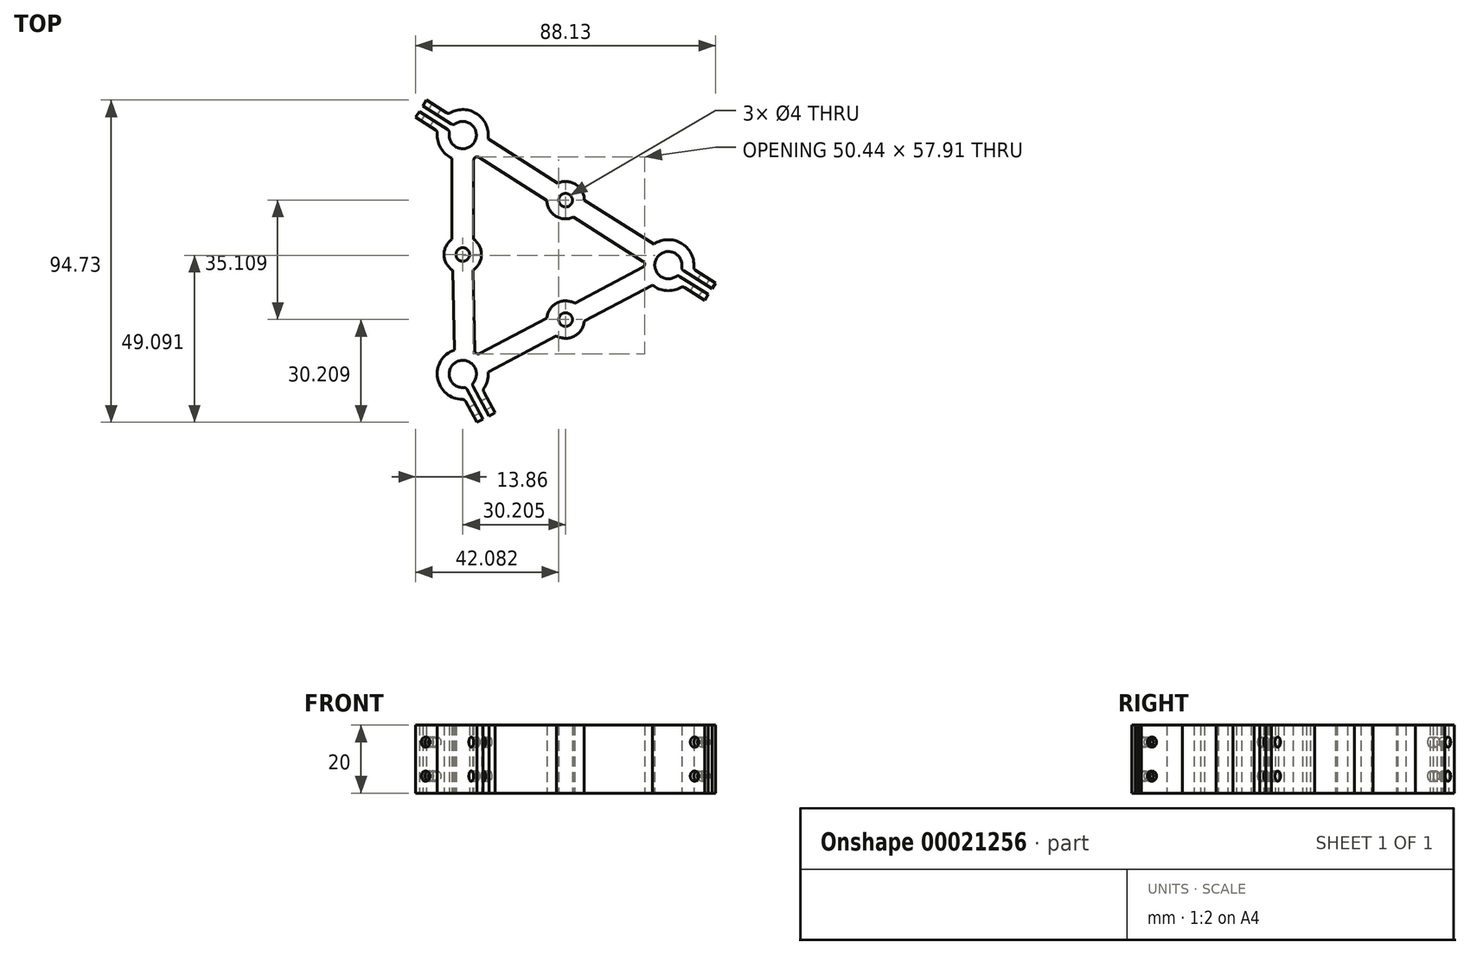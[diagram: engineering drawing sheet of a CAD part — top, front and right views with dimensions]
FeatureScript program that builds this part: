
annotation { "Feature Type Name" : "Feature", "Feature Type Description" : "" }
export const myFeature = defineFeature(function(context is Context, id is Id, definition is map)
    precondition{}
    {
        {
            var Q0;
            Q0=qCreatedBy(makeId("Top.planeOp"),FACE);
            var sketch = newSketch(context, id + "F0", { "sketchPlane" : qUnion([Q0])});
            skArc(sketch, "E0.0", {"start": v(64.36, 31.37) * mm, "mid": v(57.03, 34.12) * mm, "end": v(62.65, 28.66) * mm});
            skLineSegment(sketch, "E1", {"start": v(0, 0) * mm, "end": v(60.41, 31.98) * mm, "construction": true});
            skArc(sketch, "E2", {"start": v(3.13, -2.5) * mm, "mid": v(-1.87, 3.54) * mm, "end": v(0.3, -3.99) * mm});
            skArc(sketch, "E3", {"start": v(-3.95, 70.83) * mm, "mid": v(3.38, 68.08) * mm, "end": v(-2.24, 73.53) * mm});
            skLineSegment(sketch, "E4", {"start": v(60.41, 31.98) * mm, "end": v(0, 70.22) * mm, "construction": true});
            skCircle(sketch, "E5.0", {"center": v(30.2, 15.99) * mm, "radius": 2 * mm});
            skCircle(sketch, "E6.0", {"center": v(30.2, 51.1) * mm, "radius": 2 * mm});
            skArc(sketch, "E7.0", {"start": v(35.7, 51.17) * mm, "mid": v(33.15, 55.75) * mm, "end": v(27.91, 56.1) * mm});
            skLineSegment(sketch, "E8.0", {"start": v(56.2, 38.19) * mm, "end": v(35.7, 51.17) * mm});
            skLineSegment(sketch, "E9.0", {"start": v(52.98, 33.13) * mm, "end": v(32.5, 46.1) * mm});
            skArc(sketch, "E10.0", {"start": v(24.7, 51.03) * mm, "mid": v(27.26, 46.45) * mm, "end": v(32.5, 46.1) * mm});
            skLineSegment(sketch, "E11.0", {"start": v(24.7, 51.03) * mm, "end": v(4.73, 63.67) * mm});
            skLineSegment(sketch, "E12.0", {"start": v(27.91, 56.1) * mm, "end": v(7.41, 69.08) * mm});
            skLineSegment(sketch, "E13.0", {"start": v(7.48, 0.56) * mm, "end": v(27.53, 11.18) * mm});
            skArc(sketch, "E14.0", {"start": v(27.53, 11.18) * mm, "mid": v(32.78, 11.13) * mm, "end": v(35.68, 15.5) * mm});
            skArc(sketch, "E15.0", {"start": v(32.88, 20.8) * mm, "mid": v(27.63, 20.85) * mm, "end": v(24.73, 16.48) * mm});
            skLineSegment(sketch, "E16.0", {"start": v(35.68, 15.5) * mm, "end": v(55.74, 26.11) * mm});
            skLineSegment(sketch, "E17.0", {"start": v(52.91, 31.4) * mm, "end": v(32.88, 20.8) * mm});
            skLineSegment(sketch, "E18.0", {"start": v(-3, 30.5) * mm, "end": v(-2.5, 7.07) * mm});
            skArc(sketch, "E19.0", {"start": v(-3.2, 39.58) * mm, "mid": v(-5.5, 35) * mm, "end": v(-3, 30.5) * mm});
            skLineSegment(sketch, "E20.0", {"start": v(3.2, 39.58) * mm, "end": v(3.2, 62.83) * mm});
            skArc(sketch, "E21.0", {"start": v(3, 30.5) * mm, "mid": v(5.5, 35) * mm, "end": v(3.2, 39.58) * mm});
            skLineSegment(sketch, "E22.0", {"start": v(3.51, 6.9) * mm, "end": v(3, 30.5) * mm});
            skLineSegment(sketch, "E23", {"start": v(24.73, 16.48) * mm, "end": v(4.98, 6.03) * mm});
            skCircle(sketch, "E24.0", {"center": v(0, 35.1) * mm, "radius": 2 * mm});
            skLineSegment(sketch, "E25", {"start": v(0, 0) * mm, "end": v(0, 70.22) * mm, "construction": true});
            skLineSegment(sketch, "E26", {"start": v(64.82, 30.37) * mm, "end": v(73.2, 25.07) * mm});
            skLineSegment(sketch, "E27", {"start": v(73.2, 25.07) * mm, "end": v(74.27, 26.76) * mm});
            skLineSegment(sketch, "E28", {"start": v(74.27, 26.76) * mm, "end": v(68.35, 30.5) * mm});
            skLineSegment(sketch, "E29", {"start": v(63.75, 28.68) * mm, "end": v(72.13, 23.38) * mm});
            skLineSegment(sketch, "E30", {"start": v(72.13, 23.38) * mm, "end": v(71.06, 21.69) * mm});
            skLineSegment(sketch, "E31", {"start": v(71.06, 21.69) * mm, "end": v(65.14, 25.43) * mm});
            skLineSegment(sketch, "E32", {"start": v(6.16, -5.23) * mm, "end": v(9.44, -11.41) * mm});
            skLineSegment(sketch, "E33", {"start": v(9.44, -11.41) * mm, "end": v(7.67, -12.35) * mm});
            skLineSegment(sketch, "E34", {"start": v(7.67, -12.35) * mm, "end": v(3.03, -3.58) * mm});
            skLineSegment(sketch, "E35", {"start": v(0.86, -8.03) * mm, "end": v(4.13, -14.22) * mm});
            skLineSegment(sketch, "E36", {"start": v(4.13, -14.22) * mm, "end": v(5.9, -13.28) * mm});
            skLineSegment(sketch, "E37", {"start": v(5.9, -13.28) * mm, "end": v(1.26, -4.52) * mm});
            skLineSegment(sketch, "E38", {"start": v(-7.94, 71.7) * mm, "end": v(-13.86, 75.44) * mm});
            skLineSegment(sketch, "E39", {"start": v(-13.86, 75.44) * mm, "end": v(-12.79, 77.13) * mm});
            skLineSegment(sketch, "E40", {"start": v(-11.72, 78.82) * mm, "end": v(-10.65, 80.5) * mm});
            skLineSegment(sketch, "E41", {"start": v(-10.65, 80.5) * mm, "end": v(-4.73, 76.77) * mm});
            skLineSegment(sketch, "E42", {"start": v(0, 0) * mm, "end": v(6.78, -12.82) * mm, "construction": true});
            skArc(sketch, "E43", {"start": v(-3.34, 73.51) * mm, "mid": v(-2.79, 73.36) * mm, "end": v(-2.24, 73.53) * mm});
            skLineSegment(sketch, "E44", {"start": v(-3.34, 73.51) * mm, "end": v(-11.72, 78.82) * mm});
            skArc(sketch, "E45", {"start": v(-3.95, 70.83) * mm, "mid": v(-4.03, 71.4) * mm, "end": v(-4.4, 71.82) * mm});
            skLineSegment(sketch, "E46", {"start": v(-4.4, 71.82) * mm, "end": v(-12.79, 77.13) * mm});
            skPoint(sketch, "E47.visualSharp", {"position": v(64.22, 30.75) * mm});
            skArc(sketch, "E47.filletArc", {"start": v(64.36, 31.37) * mm, "mid": v(64.44, 30.8) * mm, "end": v(64.82, 30.37) * mm});
            skPoint(sketch, "E48.visualSharp", {"position": v(63.15, 29.06) * mm});
            skArc(sketch, "E48.filletArc", {"start": v(63.75, 28.68) * mm, "mid": v(63.2, 28.84) * mm, "end": v(62.65, 28.66) * mm});
            skArc(sketch, "E49.filletArc", {"start": v(1.26, -4.52) * mm, "mid": v(0.86, -4.11) * mm, "end": v(0.3, -3.99) * mm});
            skArc(sketch, "E50.filletArc", {"start": v(3.13, -2.5) * mm, "mid": v(2.92, -3.02) * mm, "end": v(3.03, -3.58) * mm});
            skArc(sketch, "E51.filletArc", {"start": v(6.22, -4.2) * mm, "mid": v(6.05, -4.7) * mm, "end": v(6.16, -5.23) * mm});
            skArc(sketch, "E52.filletArc", {"start": v(0.86, -8.03) * mm, "mid": v(0.5, -7.64) * mm, "end": v(-0.02, -7.5) * mm});
            skArc(sketch, "E53.filletArc", {"start": v(3.51, 6.9) * mm, "mid": v(4, 6.05) * mm, "end": v(4.98, 6.03) * mm});
            skArc(sketch, "E54.filletArc", {"start": v(4.73, 63.67) * mm, "mid": v(3.72, 63.7) * mm, "end": v(3.2, 62.83) * mm});
            skArc(sketch, "E55.filletArc", {"start": v(-7.48, 70.78) * mm, "mid": v(-7.58, 71.3) * mm, "end": v(-7.94, 71.7) * mm});
            skArc(sketch, "E56.filletArc", {"start": v(-4.73, 76.77) * mm, "mid": v(-4.22, 76.61) * mm, "end": v(-3.7, 76.74) * mm});
            skPoint(sketch, "E57.visualSharp", {"position": v(52.91, 31.4) * mm});
            skArc(sketch, "E58.filletArc", {"start": v(67.89, 31.42) * mm, "mid": v(68, 30.9) * mm, "end": v(68.35, 30.5) * mm});
            skArc(sketch, "E59.filletArc", {"start": v(65.14, 25.43) * mm, "mid": v(64.63, 25.59) * mm, "end": v(64.11, 25.46) * mm});
            skArc(sketch, "E60.filletArc", {"start": v(52.91, 31.4) * mm, "mid": v(53.44, 32.25) * mm, "end": v(52.98, 33.13) * mm});
            skLineSegment(sketch, "E61", {"start": v(-3.2, 39.58) * mm, "end": v(-3.2, 63.43) * mm});
            skArc(sketch, "E62", {"start": v(-7.48, 70.78) * mm, "mid": v(-6.48, 66.44) * mm, "end": v(-3.2, 63.43) * mm});
            skArc(sketch, "E63", {"start": v(7.41, 69.08) * mm, "mid": v(4.26, 76.4) * mm, "end": v(-3.7, 76.74) * mm});
            skArc(sketch, "E64", {"start": v(55.74, 26.11) * mm, "mid": v(59.83, 24.5) * mm, "end": v(64.11, 25.46) * mm});
            skArc(sketch, "E65", {"start": v(67.89, 31.42) * mm, "mid": v(64.17, 38.47) * mm, "end": v(56.2, 38.19) * mm});
            skArc(sketch, "E66", {"start": v(-2.5, 7.07) * mm, "mid": v(-7.4, -1.25) * mm, "end": v(-0.02, -7.5) * mm});
            skArc(sketch, "E67", {"start": v(6.22, -4.2) * mm, "mid": v(7.25, -1.92) * mm, "end": v(7.48, 0.56) * mm});
            skPoint(sketch, "E68", {"position": v(-26.15, 6.67) * mm});
            skLineSegment(sketch, "E69", {"start": v(-41.67, 32.82) * mm, "end": v(0, 22.19) * mm, "construction": true});
            skLineSegment(sketch, "E70", {"start": v(0, 22.19) * mm, "end": v(-10.63, -19.48) * mm, "construction": true});
            skLineSegment(sketch, "E71", {"start": v(-10.63, -19.48) * mm, "end": v(-52.3, -8.85) * mm, "construction": true});
            skLineSegment(sketch, "E72", {"start": v(-52.3, -8.85) * mm, "end": v(-41.67, 32.82) * mm, "construction": true});
            skLineSegment(sketch, "E73", {"start": v(-41.67, 32.82) * mm, "end": v(-10.63, -19.48) * mm, "construction": true});
            skLineSegment(sketch, "E74", {"start": v(-52.3, -8.85) * mm, "end": v(0, 22.19) * mm, "construction": true});
            skLineSegment(sketch, "E75", {"start": v(-26.15, 6.67) * mm, "end": v(0, 0) * mm, "construction": true});
            skSolve(sketch);
        }
        {
            var Q0;
            Q0=qSketchRegion(id+"F0",true);
            extrude(context, id + "F1", {"entities" : qUnion([Q0]), "depth" : 20 * mm});
        }
        {
            var Q0;
            Q0=makeQuery(id+"F1.opExtrude","SWEPT_FACE",FACE,{"disambiguationData":[OSD([sQuery(id+"F0.wireOp",EDGE,"E32")])]});
            var sketch = newSketch(context, id + "F2", { "sketchPlane" : qUnion([Q0])});
            skPoint(sketch, "E76", {"position": v(-46.16, -122.58) * mm});
            skPoint(sketch, "E77.0", {"position": v(-14.5, 20) * mm});
            skLineSegment(sketch, "E78", {"start": v(-11, 0) * mm, "end": v(-11, 10) * mm, "construction": true});
            skLineSegment(sketch, "E79", {"start": v(-11, 10) * mm, "end": v(-11, 20) * mm, "construction": true});
            skCircle(sketch, "E80", {"center": v(-11, 5) * mm, "radius": 1.5 * mm});
            skCircle(sketch, "E81", {"center": v(-11, 15) * mm, "radius": 1.5 * mm});
            skLineSegment(sketch, "E82.0", {"start": v(-7.5, 0) * mm, "end": v(-14.5, 0) * mm, "construction": true});
            skSolve(sketch);
        }
        {
            var Q0;
            Q0=sQuery(id+"F2.wireOp",VERTEX,"E81.center");
            var Q1;
            Q1=sQuery(id+"F2.wireOp",VERTEX,"E80.center");
            var Q2;
            Q2=sQuery(id+"F2.wireOp",VERTEX,"d46a1de6-ebb1-4727-ba86-f248a99db24c.center");
            var Q3;
            Q3=sQuery(id+"F2.wireOp",VERTEX,"4c406818-b156-4027-a812-089c07ca2ce7.center");
            var Q4;
            Q4=makeQuery(id+"F1.opExtrude","SWEPT_BODY",BODY,{"disambiguationData":[OSD([sQuery(id+"F0.wireOp",EDGE,"d15b060c-b4e7-47c1-8b3f-4169dc26ac33.0"),sQuery(id+"F0.wireOp",EDGE,"b688ce2c-7079-4e82-a6f3-e7d8edc49160.0"),sQuery(id+"F0.wireOp",EDGE,"E0.0"),sQuery(id+"F0.wireOp",EDGE,"E2"),sQuery(id+"F0.wireOp",EDGE,"179cd013-df81-4d8c-a0dd-ea0839fc3b2d"),sQuery(id+"F0.wireOp",EDGE,"d6a3c962-7a0e-4f93-bb74-f0ac663b7ce5"),sQuery(id+"F0.wireOp",EDGE,"bd9f0339-fb0b-4fc2-b587-6424de8abeee.0"),sQuery(id+"F0.wireOp",EDGE,"E3"),sQuery(id+"F0.wireOp",EDGE,"a22b77d8-8dfe-402b-b4b2-367bd5c247c8"),sQuery(id+"F0.wireOp",EDGE,"6933c442-a28c-4236-be47-d87d0aaef39f"),sQuery(id+"F0.wireOp",EDGE,"c0744bb6-5f96-494a-b66f-d9ae2674d7be"),sQuery(id+"F0.wireOp",EDGE,"E5.0"),sQuery(id+"F0.wireOp",EDGE,"E6.0"),sQuery(id+"F0.wireOp",EDGE,"E7.0"),sQuery(id+"F0.wireOp",EDGE,"E8.0"),sQuery(id+"F0.wireOp",EDGE,"E9.0"),sQuery(id+"F0.wireOp",EDGE,"E10.0"),sQuery(id+"F0.wireOp",EDGE,"E11.0"),sQuery(id+"F0.wireOp",EDGE,"E12.0"),sQuery(id+"F0.wireOp",EDGE,"E13.0"),sQuery(id+"F0.wireOp",EDGE,"E14.0"),sQuery(id+"F0.wireOp",EDGE,"E15.0"),sQuery(id+"F0.wireOp",EDGE,"E16.0"),sQuery(id+"F0.wireOp",EDGE,"E17.0"),sQuery(id+"F0.wireOp",EDGE,"E18.0"),sQuery(id+"F0.wireOp",EDGE,"E19.0"),sQuery(id+"F0.wireOp",EDGE,"1c8476c0-f6f5-41aa-901d-891a80c6f9dd.0"),sQuery(id+"F0.wireOp",EDGE,"E20.0"),sQuery(id+"F0.wireOp",EDGE,"E21.0"),sQuery(id+"F0.wireOp",EDGE,"E22.0"),sQuery(id+"F0.wireOp",EDGE,"E23"),sQuery(id+"F0.wireOp",EDGE,"0d48d900-cdea-47b0-8630-00f80b152a06"),sQuery(id+"F0.wireOp",EDGE,"E24.0"),sQuery(id+"F0.wireOp",EDGE,"24b9ab60-6409-4e19-94a0-6aad9d850b7f"),sQuery(id+"F0.wireOp",EDGE,"5e6aeb22-7271-4e21-90b8-9b21e77531b6"),sQuery(id+"F0.wireOp",EDGE,"041c5739-6fd8-4943-8542-bfcab8119015")])]});
            hole(context, id + "F3", {"style" : HoleStyle.SIMPLE, "holeDiameter" : 3 * mm, "endStyle" : HoleEndStyle.BLIND, "holeDepth" : 6 * mm, "locations" : qUnion([Q0, Q1, Q2, Q3]), "scope" : qUnion([Q4])});
        }
        {
            var Q0;
            Q0=makeQuery(id+"F1.opExtrude","SWEPT_FACE",FACE,{"disambiguationData":[OSD([sQuery(id+"F0.wireOp",EDGE,"E28")])]});
            var sketch = newSketch(context, id + "F4", { "sketchPlane" : qUnion([Q0])});
            skCircle(sketch, "E83", {"center": v(-44.94, 15) * mm, "radius": 1.5 * mm});
            skCircle(sketch, "E84", {"center": v(-44.94, 5) * mm, "radius": 1.5 * mm});
            skLineSegment(sketch, "E85.0", {"start": v(-48.44, 20) * mm, "end": v(-48.44, 20) * mm});
            skLineSegment(sketch, "E86.0", {"start": v(-48.44, 0) * mm, "end": v(-48.44, 0) * mm});
            skLineSegment(sketch, "E87", {"start": v(-44.94, 0) * mm, "end": v(-44.94, 10) * mm, "construction": true});
            skLineSegment(sketch, "E88", {"start": v(-44.94, 10) * mm, "end": v(-44.94, 20) * mm, "construction": true});
            skLineSegment(sketch, "E89.0", {"start": v(-48.44, 0) * mm, "end": v(-41.44, 0) * mm, "construction": true});
            skLineSegment(sketch, "E90.0", {"start": v(45.06, 0) * mm, "end": v(52.06, 0) * mm, "construction": true});
            skLineSegment(sketch, "E91", {"start": v(48.56, 0) * mm, "end": v(48.56, 20) * mm, "construction": true});
            skCircle(sketch, "E92", {"center": v(48.56, 15) * mm, "radius": 1.5 * mm});
            skCircle(sketch, "E93", {"center": v(48.56, 5) * mm, "radius": 1.5 * mm});
            skSolve(sketch);
        }
        {
            var Q0;
            Q0=sQuery(id+"F4.wireOp",VERTEX,"E83.center");
            var Q1;
            Q1=sQuery(id+"F4.wireOp",VERTEX,"E84.center");
            var Q2;
            Q2=sQuery(id+"F4.wireOp",VERTEX,"E92.center");
            var Q3;
            Q3=sQuery(id+"F4.wireOp",VERTEX,"E93.center");
            var Q4;
            Q4=makeQuery(id+"F1.opExtrude","SWEPT_BODY",BODY,{"disambiguationData":[OSD([sQuery(id+"F0.wireOp",EDGE,"d15b060c-b4e7-47c1-8b3f-4169dc26ac33.0"),sQuery(id+"F0.wireOp",EDGE,"b688ce2c-7079-4e82-a6f3-e7d8edc49160.0"),sQuery(id+"F0.wireOp",EDGE,"E0.0"),sQuery(id+"F0.wireOp",EDGE,"E2"),sQuery(id+"F0.wireOp",EDGE,"179cd013-df81-4d8c-a0dd-ea0839fc3b2d"),sQuery(id+"F0.wireOp",EDGE,"d6a3c962-7a0e-4f93-bb74-f0ac663b7ce5"),sQuery(id+"F0.wireOp",EDGE,"bd9f0339-fb0b-4fc2-b587-6424de8abeee.0"),sQuery(id+"F0.wireOp",EDGE,"E3"),sQuery(id+"F0.wireOp",EDGE,"a22b77d8-8dfe-402b-b4b2-367bd5c247c8"),sQuery(id+"F0.wireOp",EDGE,"6933c442-a28c-4236-be47-d87d0aaef39f"),sQuery(id+"F0.wireOp",EDGE,"c0744bb6-5f96-494a-b66f-d9ae2674d7be"),sQuery(id+"F0.wireOp",EDGE,"E5.0"),sQuery(id+"F0.wireOp",EDGE,"E6.0"),sQuery(id+"F0.wireOp",EDGE,"E7.0"),sQuery(id+"F0.wireOp",EDGE,"E8.0"),sQuery(id+"F0.wireOp",EDGE,"E9.0"),sQuery(id+"F0.wireOp",EDGE,"E10.0"),sQuery(id+"F0.wireOp",EDGE,"E11.0"),sQuery(id+"F0.wireOp",EDGE,"E12.0"),sQuery(id+"F0.wireOp",EDGE,"E13.0"),sQuery(id+"F0.wireOp",EDGE,"E14.0"),sQuery(id+"F0.wireOp",EDGE,"E15.0"),sQuery(id+"F0.wireOp",EDGE,"E16.0"),sQuery(id+"F0.wireOp",EDGE,"E17.0"),sQuery(id+"F0.wireOp",EDGE,"E18.0"),sQuery(id+"F0.wireOp",EDGE,"E19.0"),sQuery(id+"F0.wireOp",EDGE,"1c8476c0-f6f5-41aa-901d-891a80c6f9dd.0"),sQuery(id+"F0.wireOp",EDGE,"E20.0"),sQuery(id+"F0.wireOp",EDGE,"E21.0"),sQuery(id+"F0.wireOp",EDGE,"E22.0"),sQuery(id+"F0.wireOp",EDGE,"E23"),sQuery(id+"F0.wireOp",EDGE,"0d48d900-cdea-47b0-8630-00f80b152a06"),sQuery(id+"F0.wireOp",EDGE,"E24.0"),sQuery(id+"F0.wireOp",EDGE,"24b9ab60-6409-4e19-94a0-6aad9d850b7f"),sQuery(id+"F0.wireOp",EDGE,"5e6aeb22-7271-4e21-90b8-9b21e77531b6"),sQuery(id+"F0.wireOp",EDGE,"041c5739-6fd8-4943-8542-bfcab8119015")])]});
            hole(context, id + "F5", {"style" : HoleStyle.SIMPLE, "holeDiameter" : 3 * mm, "endStyle" : HoleEndStyle.BLIND, "holeDepth" : 8 * mm, "locations" : qUnion([Q0, Q1, Q2, Q3]), "scope" : qUnion([Q4])});
        }
    });
